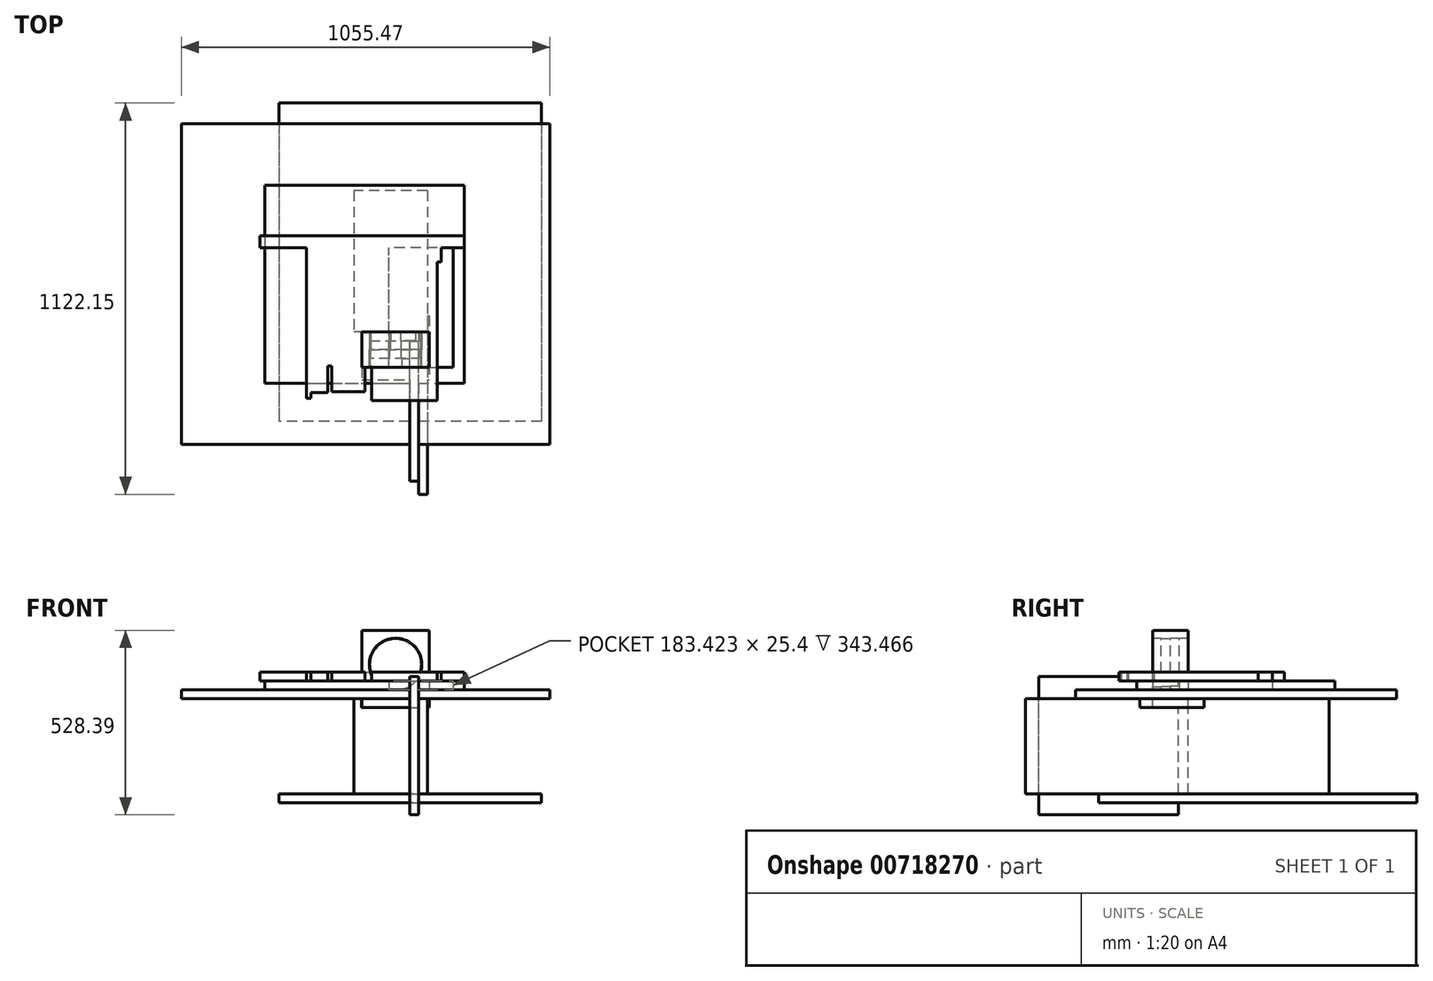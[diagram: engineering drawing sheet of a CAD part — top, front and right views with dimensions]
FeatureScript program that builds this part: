
annotation { "Feature Type Name" : "Feature", "Feature Type Description" : "" }
export const myFeature = defineFeature(function(context is Context, id is Id, definition is map)
    precondition{}
    {
        {
            var Q0;
            Q0=qCreatedBy(makeId("Front.planeOp"),FACE);
            var sketch = newSketch(context, id + "F0", { "sketchPlane" : qUnion([Q0])});
            skCircle(sketch, "E0", {"center": v(0, 0) * mm, "radius": 74.89 * mm});
            skLineSegment(sketch, "E1.bottom", {"start": v(-96.7, 97.65) * mm, "end": v(96.69, 97.65) * mm});
            skLineSegment(sketch, "E1.top", {"start": v(-96.7, -98.4) * mm, "end": v(96.69, -98.4) * mm});
            skLineSegment(sketch, "E1.left", {"start": v(-96.7, 97.65) * mm, "end": v(-96.7, -98.4) * mm});
            skLineSegment(sketch, "E1.right", {"start": v(96.69, 97.65) * mm, "end": v(96.69, -98.4) * mm});
            skSolve(sketch);
        }
        {
            var Q0;
            Q0 = qSketchRegion(id + "F0", true);
            extrude(context, id + "F1", {"entities" : qUnion([Q0]), "depth" : 25.4 * mm, "offsetDistance" : 25.4 * mm});
        }
        {
            var Q0;
            Q0=makeQuery(id+"F1.opExtrude","CAP_FACE",FACE,{"disambiguationData":[OSD([sQuery(id+"F0.wireOp",EDGE,"E0"),sQuery(id+"F0.wireOp",EDGE,"E1.bottom"),sQuery(id+"F0.wireOp",EDGE,"E1.top"),sQuery(id+"F0.wireOp",EDGE,"E1.left"),sQuery(id+"F0.wireOp",EDGE,"E1.right")])],"isStart":true});
            var sketch = newSketch(context, id + "F2", { "sketchPlane" : qUnion([Q0])});
            skLineSegment(sketch, "E2.bottom", {"start": v(96.7, 97.65) * mm, "end": v(-96.69, 97.65) * mm});
            skLineSegment(sketch, "E2.top", {"start": v(96.7, -98.4) * mm, "end": v(-96.69, -98.4) * mm});
            skLineSegment(sketch, "E2.left", {"start": v(96.7, 97.65) * mm, "end": v(96.7, -98.4) * mm});
            skLineSegment(sketch, "E2.right", {"start": v(-96.69, 97.65) * mm, "end": v(-96.69, -98.4) * mm});
            skCircle(sketch, "E3", {"center": v(0, 0) * mm, "radius": 74.66 * mm});
            skSolve(sketch);
        }
        {
            var Q0;
            Q0 = qSketchRegion(id + "F2", true);
            extrude(context, id + "F3", {"entities" : qUnion([Q0]), "operationType" : NewBodyOperationType.ADD, "depth" : 25.4 * mm, "offsetDistance" : 25.4 * mm});
        }
        {
            var Q0;
            Q0=makeQuery(id+"F3.opExtrude","CAP_FACE",FACE,{"disambiguationData":[OSD([sQuery(id+"F2.wireOp",EDGE,"E2.bottom"),sQuery(id+"F2.wireOp",EDGE,"E2.top"),sQuery(id+"F2.wireOp",EDGE,"E2.left"),sQuery(id+"F2.wireOp",EDGE,"E2.right"),sQuery(id+"F2.wireOp",EDGE,"E3")])],"isStart":false});
            var sketch = newSketch(context, id + "F4", { "sketchPlane" : qUnion([Q0])});
            skLineSegment(sketch, "E4.bottom", {"start": v(-96.69, 97.65) * mm, "end": v(96.7, 97.65) * mm});
            skLineSegment(sketch, "E4.top", {"start": v(-96.69, -98.4) * mm, "end": v(96.7, -98.4) * mm});
            skLineSegment(sketch, "E4.left", {"start": v(-96.69, 97.65) * mm, "end": v(-96.69, -98.4) * mm});
            skLineSegment(sketch, "E4.right", {"start": v(96.7, 97.65) * mm, "end": v(96.7, -98.4) * mm});
            skCircle(sketch, "E5", {"center": v(0, 0) * mm, "radius": 74.39 * mm});
            skLineSegment(sketch, "E6.bottom", {"start": v(-96.69, 97.65) * mm, "end": v(79.45, 97.65) * mm});
            skLineSegment(sketch, "E6.top", {"start": v(-96.69, -98.4) * mm, "end": v(79.45, -98.4) * mm});
            skLineSegment(sketch, "E6.right", {"start": v(79.45, 97.65) * mm, "end": v(79.45, -98.4) * mm});
            skSolve(sketch);
        }
        {
            var Q0;
            Q0 = qSketchRegion(id + "F4", true);
            extrude(context, id + "F5", {"entities" : qUnion([Q0]), "operationType" : NewBodyOperationType.ADD, "depth" : 25.4 * mm, "offsetDistance" : 25.4 * mm});
        }
        {
            var Q0;
            Q0=makeQuery(id+"F1.opExtrude","CAP_FACE",FACE,{"disambiguationData":[OSD([sQuery(id+"F0.wireOp",EDGE,"E0"),sQuery(id+"F0.wireOp",EDGE,"E1.bottom"),sQuery(id+"F0.wireOp",EDGE,"E1.top"),sQuery(id+"F0.wireOp",EDGE,"E1.left"),sQuery(id+"F0.wireOp",EDGE,"E1.right")])],"isStart":false});
            var sketch = newSketch(context, id + "F6", { "sketchPlane" : qUnion([Q0])});
            skCircle(sketch, "E7", {"center": v(0, 0) * mm, "radius": 75.35 * mm});
            skLineSegment(sketch, "E8.bottom", {"start": v(96.69, -98.4) * mm, "end": v(-96.7, -98.4) * mm});
            skLineSegment(sketch, "E8.top", {"start": v(96.69, 97.65) * mm, "end": v(-96.7, 97.65) * mm});
            skLineSegment(sketch, "E8.left", {"start": v(96.69, -98.4) * mm, "end": v(96.69, 97.65) * mm});
            skLineSegment(sketch, "E8.right", {"start": v(-96.7, -98.4) * mm, "end": v(-96.7, 97.65) * mm});
            skSolve(sketch);
        }
        {
            var Q0;
            Q0 = qSketchRegion(id + "F6", true);
            extrude(context, id + "F7", {"entities" : qUnion([Q0]), "operationType" : NewBodyOperationType.ADD, "depth" : 25.4 * mm, "offsetDistance" : 25.4 * mm});
        }
        {
            var Q0;
            Q0=makeQuery(id+"F7.boolean.opBoolean","MERGE",FACE,{"derivedFrom":[makeQuery(id+"F5.boolean.opBoolean","MERGE",FACE,{"derivedFrom":[makeQuery(id+"F3.boolean.opBoolean","MERGE",FACE,{"derivedFrom":[makeQuery(id+"F1.opExtrude","SWEPT_FACE",FACE,{"disambiguationData":[OSD([sQuery(id+"F0.wireOp",EDGE,"E1.top")])]}),makeQuery(id+"F3.opExtrude","SWEPT_FACE",FACE,{"disambiguationData":[OSD([sQuery(id+"F2.wireOp",EDGE,"E2.top")])]})]}),makeQuery(id+"F5.opExtrude","SWEPT_FACE",FACE,{"disambiguationData":[OSD([sQuery(id+"F4.wireOp",EDGE,"E4.top"),sQuery(id+"F4.wireOp",EDGE,"E6.top")])]})]}),makeQuery(id+"F7.opExtrude","SWEPT_FACE",FACE,{"disambiguationData":[OSD([sQuery(id+"F6.wireOp",EDGE,"E8.bottom")])]})]});
            var sketch = newSketch(context, id + "F8", { "sketchPlane" : qUnion([Q0])});
            skLineSegment(sketch, "E9.bottom", {"start": v(-96.7, 50.8) * mm, "end": v(96.76, 50.8) * mm});
            skLineSegment(sketch, "E9.top", {"start": v(-96.7, 86.52) * mm, "end": v(96.76, 86.52) * mm});
            skLineSegment(sketch, "E9.left", {"start": v(-96.7, 50.8) * mm, "end": v(-96.7, 86.52) * mm});
            skLineSegment(sketch, "E9.right", {"start": v(96.76, 50.8) * mm, "end": v(96.76, 86.52) * mm});
            skLineSegment(sketch, "E10.bottom", {"start": v(96.76, 50.8) * mm, "end": v(-97.9, 50.8) * mm});
            skLineSegment(sketch, "E10.top", {"start": v(96.76, -97.27) * mm, "end": v(-97.9, -97.27) * mm});
            skLineSegment(sketch, "E10.left", {"start": v(96.76, 50.8) * mm, "end": v(96.76, -97.27) * mm});
            skLineSegment(sketch, "E10.right", {"start": v(-97.9, 50.8) * mm, "end": v(-97.9, -97.27) * mm});
            skSolve(sketch);
        }
        {
            var Q0;
            Q0 = qSketchRegion(id + "F8", true);
            extrude(context, id + "F9", {"entities" : qUnion([Q0]), "operationType" : NewBodyOperationType.ADD, "depth" : 25.4 * mm, "offsetDistance" : 25.4 * mm});
        }
        {
            var Q0;
            Q0=makeQuery(id+"F5.opExtrude","CAP_FACE",FACE,{"disambiguationData":[OSD([sQuery(id+"F4.wireOp",EDGE,"E4.bottom"),sQuery(id+"F4.wireOp",EDGE,"E4.top"),sQuery(id+"F4.wireOp",EDGE,"E4.right"),sQuery(id+"F4.wireOp",EDGE,"E5"),sQuery(id+"F4.wireOp",EDGE,"E6.bottom"),sQuery(id+"F4.wireOp",EDGE,"E6.top"),sQuery(id+"F4.wireOp",EDGE,"E4.left")])],"isStart":false});
            var sketch = newSketch(context, id + "F10", { "sketchPlane" : qUnion([Q0])});
            skPoint(sketch, "E11.oppositeSnap0", {"position": v(0, -98.4) * mm});
            skLineSegment(sketch, "E11.bottom", {"start": v(-65.78, -371.3) * mm, "end": v(119.1, -371.3) * mm});
            skLineSegment(sketch, "E11.top", {"start": v(-65.78, -98.4) * mm, "end": v(119.1, -98.4) * mm});
            skLineSegment(sketch, "E11.left", {"start": v(-65.78, -371.3) * mm, "end": v(-65.78, -98.4) * mm});
            skLineSegment(sketch, "E11.right", {"start": v(119.1, -371.3) * mm, "end": v(119.1, -98.4) * mm});
            skLineSegment(sketch, "E12.bottom", {"start": v(-65.78, -98.4) * mm, "end": v(-65.78, -98.4) * mm});
            skLineSegment(sketch, "E12.top", {"start": v(-65.78, -350.33) * mm, "end": v(-65.78, -350.33) * mm});
            skLineSegment(sketch, "E12.left", {"start": v(-65.78, -98.4) * mm, "end": v(-65.78, -350.33) * mm});
            skLineSegment(sketch, "E12.right", {"start": v(-65.78, -98.4) * mm, "end": v(-65.78, -350.33) * mm});
            skSolve(sketch);
        }
        {
            var Q0;
            Q0 = qSketchRegion(id + "F10", true);
            extrude(context, id + "F11", {"entities" : qUnion([Q0]), "operationType" : NewBodyOperationType.ADD, "depth" : 404.62 * mm, "offsetDistance" : 25.4 * mm});
        }
        {
            var Q0;
            Q0=makeQuery(id+"F11.boolean.opBoolean","MERGE",FACE,{"derivedFrom":[makeQuery(id+"F9.opExtrude","CAP_FACE",FACE,{"disambiguationData":[OSD([sQuery(id+"F8.wireOp",EDGE,"E9.top"),sQuery(id+"F8.wireOp",EDGE,"E9.left"),sQuery(id+"F8.wireOp",EDGE,"E9.right"),sQuery(id+"F8.wireOp",EDGE,"E10.bottom"),sQuery(id+"F8.wireOp",EDGE,"E10.top"),sQuery(id+"F8.wireOp",EDGE,"E10.left"),sQuery(id+"F8.wireOp",EDGE,"E10.right")])],"isStart":true}),makeQuery(id+"F11.opExtrude","SWEPT_FACE",FACE,{"disambiguationData":[OSD([sQuery(id+"F10.wireOp",EDGE,"E11.top")])]})]});
            var sketch = newSketch(context, id + "F12", { "sketchPlane" : qUnion([Q0])});
            skLineSegment(sketch, "E13.bottom", {"start": v(442, 647.7) * mm, "end": v(-613.47, 647.7) * mm});
            skLineSegment(sketch, "E13.top", {"start": v(442, -271.27) * mm, "end": v(-613.47, -271.27) * mm});
            skLineSegment(sketch, "E13.left", {"start": v(442, 647.7) * mm, "end": v(442, -271.27) * mm});
            skLineSegment(sketch, "E13.right", {"start": v(-613.47, 647.7) * mm, "end": v(-613.47, -271.27) * mm});
            skSolve(sketch);
        }
        {
            var Q0;
            Q0 = qSketchRegion(id + "F12", true);
            extrude(context, id + "F13", {"entities" : qUnion([Q0]), "operationType" : NewBodyOperationType.ADD, "depth" : 25.4 * mm, "offsetDistance" : 25.4 * mm});
        }
        {
            var Q0;
            Q0=makeQuery(id+"F11.opExtrude","SWEPT_FACE",FACE,{"disambiguationData":[OSD([sQuery(id+"F10.wireOp",EDGE,"E11.bottom")])]});
            var sketch = newSketch(context, id + "F14", { "sketchPlane" : qUnion([Q0])});
            skLineSegment(sketch, "E14.bottom", {"start": v(418.46, -707.28) * mm, "end": v(-334.36, -707.28) * mm});
            skLineSegment(sketch, "E14.top", {"start": v(418.46, 205.48) * mm, "end": v(-334.36, 205.48) * mm});
            skLineSegment(sketch, "E14.left", {"start": v(418.46, -707.28) * mm, "end": v(418.46, 205.48) * mm});
            skLineSegment(sketch, "E14.right", {"start": v(-334.36, -707.28) * mm, "end": v(-334.36, 205.48) * mm});
            skSolve(sketch);
        }
        {
            var Q0;
            Q0 = qSketchRegion(id + "F14", true);
            extrude(context, id + "F15", {"entities" : qUnion([Q0]), "operationType" : NewBodyOperationType.ADD, "depth" : 25.4 * mm, "offsetDistance" : 25.4 * mm});
        }
        {
            var Q0;
            Q0=makeQuery(id+"F11.opExtrude","SWEPT_FACE",FACE,{"disambiguationData":[OSD([sQuery(id+"F10.wireOp",EDGE,"E11.left"),sQuery(id+"F10.wireOp",EDGE,"E12.right")])]});
            var sketch = newSketch(context, id + "F16", { "sketchPlane" : qUnion([Q0])});
            skLineSegment(sketch, "E15.bottom", {"start": v(455.42, -98.4) * mm, "end": v(-414.87, -98.4) * mm});
            skLineSegment(sketch, "E15.top", {"start": v(455.42, -371.3) * mm, "end": v(-414.87, -371.3) * mm});
            skLineSegment(sketch, "E15.left", {"start": v(455.42, -98.4) * mm, "end": v(455.42, -371.3) * mm});
            skLineSegment(sketch, "E15.right", {"start": v(-414.87, -98.4) * mm, "end": v(-414.87, -371.3) * mm});
            skSolve(sketch);
        }
        {
            var Q0;
            Q0 = qSketchRegion(id + "F16", true);
            extrude(context, id + "F17", {"entities" : qUnion([Q0]), "operationType" : NewBodyOperationType.ADD, "depth" : 25.4 * mm, "offsetDistance" : 25.4 * mm});
        }
        {
            var Q0;
            Q0=makeQuery(id+"F17.opExtrude","CAP_FACE",FACE,{"disambiguationData":[OSD([sQuery(id+"F16.wireOp",EDGE,"E15.bottom"),sQuery(id+"F16.wireOp",EDGE,"E15.top"),sQuery(id+"F16.wireOp",EDGE,"E15.left"),sQuery(id+"F16.wireOp",EDGE,"E15.right")])],"isStart":true});
            var sketch = newSketch(context, id + "F18", { "sketchPlane" : qUnion([Q0])});
            skLineSegment(sketch, "E16.bottom", {"start": v(377, -430.74) * mm, "end": v(-23.69, -430.74) * mm});
            skLineSegment(sketch, "E16.top", {"start": v(377, -35.11) * mm, "end": v(-23.69, -35.11) * mm});
            skLineSegment(sketch, "E16.left", {"start": v(377, -430.74) * mm, "end": v(377, -35.11) * mm});
            skLineSegment(sketch, "E16.right", {"start": v(-23.69, -430.74) * mm, "end": v(-23.69, -35.11) * mm});
            skSolve(sketch);
        }
        {
            var Q0;
            Q0 = qSketchRegion(id + "F18", true);
            extrude(context, id + "F19", {"entities" : qUnion([Q0]), "operationType" : NewBodyOperationType.ADD, "depth" : 25.4 * mm, "offsetDistance" : 25.4 * mm});
        }
        {
            var Q0;
            Q0=makeQuery(id+"F13.opExtrude","CAP_FACE",FACE,{"disambiguationData":[OSD([sQuery(id+"F12.wireOp",EDGE,"E13.bottom"),sQuery(id+"F12.wireOp",EDGE,"E13.top"),sQuery(id+"F12.wireOp",EDGE,"E13.left"),sQuery(id+"F12.wireOp",EDGE,"E13.right")])],"isStart":false});
            var sketch = newSketch(context, id + "F20", { "sketchPlane" : qUnion([Q0])});
            skLineSegment(sketch, "E17.bottom", {"start": v(-18.7, -50.8) * mm, "end": v(129.85, -50.8) * mm});
            skLineSegment(sketch, "E17.top", {"start": v(-18.7, 275.13) * mm, "end": v(129.85, 275.13) * mm});
            skLineSegment(sketch, "E17.left", {"start": v(-18.7, -50.8) * mm, "end": v(-18.7, 275.13) * mm});
            skLineSegment(sketch, "E17.right", {"start": v(129.85, -50.8) * mm, "end": v(129.85, 275.13) * mm});
            skLineSegment(sketch, "E18.bottom", {"start": v(40.38, -50.8) * mm, "end": v(164.73, -50.8) * mm});
            skLineSegment(sketch, "E18.top", {"start": v(40.38, 292.67) * mm, "end": v(164.73, 292.67) * mm});
            skLineSegment(sketch, "E18.left", {"start": v(40.38, -50.8) * mm, "end": v(40.38, 292.67) * mm});
            skLineSegment(sketch, "E18.right", {"start": v(164.73, -50.8) * mm, "end": v(164.73, 292.67) * mm});
            skLineSegment(sketch, "E19.bottom", {"start": v(40.38, 292.67) * mm, "end": v(-18.7, 292.67) * mm});
            skLineSegment(sketch, "E19.top", {"start": v(40.38, -50.8) * mm, "end": v(-18.7, -50.8) * mm});
            skLineSegment(sketch, "E19.left", {"start": v(40.38, 292.67) * mm, "end": v(40.38, -50.8) * mm});
            skLineSegment(sketch, "E19.right", {"start": v(-18.7, 292.67) * mm, "end": v(-18.7, -50.8) * mm});
            skLineSegment(sketch, "E20.bottom", {"start": v(-374.6, 471.3) * mm, "end": v(197.19, 471.3) * mm});
            skLineSegment(sketch, "E20.top", {"start": v(-374.6, -96.06) * mm, "end": v(197.19, -96.06) * mm});
            skLineSegment(sketch, "E20.left", {"start": v(-374.6, 471.3) * mm, "end": v(-374.6, -96.06) * mm});
            skLineSegment(sketch, "E20.right", {"start": v(197.19, 471.3) * mm, "end": v(197.19, -96.06) * mm});
            skSolve(sketch);
        }
        {
            var Q0;
            Q0 = qSketchRegion(id + "F20", true);
            extrude(context, id + "F21", {"entities" : qUnion([Q0]), "operationType" : NewBodyOperationType.ADD, "depth" : 25.4 * mm, "offsetDistance" : 25.4 * mm});
        }
        {
            var Q0;
            Q0=makeQuery(id+"F21.opExtrude","CAP_FACE",FACE,{"disambiguationData":[OSD([sQuery(id+"F20.wireOp",EDGE,"E18.bottom"),sQuery(id+"F20.wireOp",EDGE,"E18.top"),sQuery(id+"F20.wireOp",EDGE,"E18.right"),sQuery(id+"F20.wireOp",EDGE,"E19.bottom"),sQuery(id+"F20.wireOp",EDGE,"E19.top"),sQuery(id+"F20.wireOp",EDGE,"E19.right"),sQuery(id+"F20.wireOp",EDGE,"E20.bottom"),sQuery(id+"F20.wireOp",EDGE,"E20.top"),sQuery(id+"F20.wireOp",EDGE,"E20.left"),sQuery(id+"F20.wireOp",EDGE,"E20.right")])],"isStart":false});
            var sketch = newSketch(context, id + "F22", { "sketchPlane" : qUnion([Q0])});
            skPoint(sketch, "E21.firstSnap0", {"position": v(-76.93, 50.8) * mm});
            skLineSegment(sketch, "E21.bottom", {"start": v(-76.93, 25.4) * mm, "end": v(112.19, 25.4) * mm});
            skLineSegment(sketch, "E21.top", {"start": v(-76.93, 292.67) * mm, "end": v(112.19, 292.67) * mm});
            skLineSegment(sketch, "E21.left", {"start": v(-76.93, 25.4) * mm, "end": v(-76.93, 292.67) * mm});
            skLineSegment(sketch, "E21.right", {"start": v(112.19, 25.4) * mm, "end": v(112.19, 292.67) * mm});
            skLineSegment(sketch, "E22.bottom", {"start": v(-57.16, 313.55) * mm, "end": v(-249.49, 313.55) * mm});
            skLineSegment(sketch, "E22.top", {"start": v(-57.16, 244) * mm, "end": v(-249.49, 244) * mm});
            skLineSegment(sketch, "E22.left", {"start": v(-57.16, 313.55) * mm, "end": v(-57.16, 244) * mm});
            skLineSegment(sketch, "E22.right", {"start": v(-249.49, 313.55) * mm, "end": v(-249.49, 244) * mm});
            skSolve(sketch);
        }
        {
            var Q0;
            {var subQ73=sQuery(id+"F22.wireOp",EDGE,"E22.bottom");Q0=makeQuery(id+"F22.imprint","IMPRINT",FACE,{"disambiguationData":[TD([[makeQuery(id+"F22.imprint","IMPRINT",EDGE,{"derivedFrom":subQ73}),-1.0]])]});}
            var sketch = newSketch(context, id + "F23", { "sketchPlane" : qUnion([Q0])});
            skLineSegment(sketch, "E23.bottom", {"start": v(119.3, 292.35) * mm, "end": v(-255.69, 292.35) * mm});
            skLineSegment(sketch, "E23.top", {"start": v(119.3, -40.38) * mm, "end": v(-255.69, -40.38) * mm});
            skLineSegment(sketch, "E23.left", {"start": v(119.3, 292.35) * mm, "end": v(119.3, -40.38) * mm});
            skLineSegment(sketch, "E23.right", {"start": v(-255.69, 292.35) * mm, "end": v(-255.69, -40.38) * mm});
            skPoint(sketch, "E24.oppositeSnap0", {"position": v(-68.2, 292.35) * mm});
            skLineSegment(sketch, "E24.bottom", {"start": v(119.3, -40.38) * mm, "end": v(-68.2, -40.38) * mm});
            skLineSegment(sketch, "E24.top", {"start": v(119.3, -146.15) * mm, "end": v(-68.2, -146.15) * mm});
            skLineSegment(sketch, "E24.left", {"start": v(119.3, -40.38) * mm, "end": v(119.3, -146.15) * mm});
            skLineSegment(sketch, "E24.right", {"start": v(-68.2, -40.38) * mm, "end": v(-68.2, -146.15) * mm});
            skLineSegment(sketch, "E25.bottom", {"start": v(-242.38, -140.03) * mm, "end": v(-255.69, -140.03) * mm});
            skLineSegment(sketch, "E25.top", {"start": v(-242.38, 292.35) * mm, "end": v(-255.69, 292.35) * mm});
            skLineSegment(sketch, "E25.left", {"start": v(-242.38, -140.03) * mm, "end": v(-242.38, 292.35) * mm});
            skLineSegment(sketch, "E25.right", {"start": v(-255.69, -140.03) * mm, "end": v(-255.69, 292.35) * mm});
            skLineSegment(sketch, "E26.bottom", {"start": v(119.3, 292.35) * mm, "end": v(197.3, 292.35) * mm});
            skLineSegment(sketch, "E26.top", {"start": v(119.3, 326.83) * mm, "end": v(197.3, 326.83) * mm});
            skLineSegment(sketch, "E26.left", {"start": v(119.3, 292.35) * mm, "end": v(119.3, 326.83) * mm});
            skLineSegment(sketch, "E26.right", {"start": v(197.3, 292.35) * mm, "end": v(197.3, 326.83) * mm});
            skLineSegment(sketch, "E27.bottom", {"start": v(119.3, 326.83) * mm, "end": v(-389.01, 326.83) * mm});
            skLineSegment(sketch, "E27.top", {"start": v(119.3, 292.35) * mm, "end": v(-389.01, 292.35) * mm});
            skLineSegment(sketch, "E27.left", {"start": v(119.3, 326.83) * mm, "end": v(119.3, 292.35) * mm});
            skLineSegment(sketch, "E27.right", {"start": v(-389.01, 326.83) * mm, "end": v(-389.01, 292.35) * mm});
            skSolve(sketch);
        }
        {
            var Q0;
            Q0 = qSketchRegion(id + "F23", true);
            extrude(context, id + "F24", {"entities" : qUnion([Q0]), "operationType" : NewBodyOperationType.ADD, "depth" : 25.4 * mm, "offsetDistance" : 25.4 * mm});
        }
        {
            var Q0;
            {var subQ73=sQuery(id+"F22.wireOp",EDGE,"E22.bottom");Q0=makeQuery(id+"F22.imprint","IMPRINT",FACE,{"disambiguationData":[TD([[makeQuery(id+"F22.imprint","IMPRINT",EDGE,{"derivedFrom":subQ73}),-1.0]])]});}
            var sketch = newSketch(context, id + "F25", { "sketchPlane" : qUnion([Q0])});
            skLineSegment(sketch, "E28.bottom", {"start": v(0, 0) * mm, "end": v(-69.9, 0) * mm});
            skLineSegment(sketch, "E28.top", {"start": v(0, 301.84) * mm, "end": v(-69.9, 301.84) * mm});
            skLineSegment(sketch, "E28.left", {"start": v(0, 0) * mm, "end": v(0, 301.84) * mm});
            skLineSegment(sketch, "E28.right", {"start": v(-69.9, 0) * mm, "end": v(-69.9, 301.84) * mm});
            skLineSegment(sketch, "E29.bottom", {"start": v(0, 301.84) * mm, "end": v(131.1, 301.84) * mm});
            skLineSegment(sketch, "E29.top", {"start": v(0, 251.58) * mm, "end": v(131.1, 251.58) * mm});
            skLineSegment(sketch, "E29.left", {"start": v(0, 301.84) * mm, "end": v(0, 251.58) * mm});
            skLineSegment(sketch, "E29.right", {"start": v(131.1, 301.84) * mm, "end": v(131.1, 251.58) * mm});
            skLineSegment(sketch, "E30.bottom", {"start": v(-69.9, 301.84) * mm, "end": v(-248.72, 301.84) * mm});
            skLineSegment(sketch, "E30.top", {"start": v(-69.9, 239.47) * mm, "end": v(-248.72, 239.47) * mm});
            skLineSegment(sketch, "E30.left", {"start": v(-69.9, 301.84) * mm, "end": v(-69.9, 239.47) * mm});
            skLineSegment(sketch, "E30.right", {"start": v(-248.72, 301.84) * mm, "end": v(-248.72, 239.47) * mm});
            skLineSegment(sketch, "E31.bottom", {"start": v(101.54, 0) * mm, "end": v(0, 0) * mm});
            skLineSegment(sketch, "E31.top", {"start": v(101.54, 301.84) * mm, "end": v(0, 301.84) * mm});
            skLineSegment(sketch, "E31.left", {"start": v(101.54, 0) * mm, "end": v(101.54, 301.84) * mm});
            skLineSegment(sketch, "E32.bottom", {"start": v(-69.9, 0) * mm, "end": v(101.54, 0) * mm});
            skLineSegment(sketch, "E32.top", {"start": v(-69.9, -46.32) * mm, "end": v(101.54, -46.32) * mm});
            skLineSegment(sketch, "E32.left", {"start": v(-69.9, 0) * mm, "end": v(-69.9, -46.32) * mm});
            skLineSegment(sketch, "E32.right", {"start": v(101.54, 0) * mm, "end": v(101.54, -46.32) * mm});
            skLineSegment(sketch, "E33.bottom", {"start": v(-69.9, -46.32) * mm, "end": v(-69.9, -46.32) * mm});
            skLineSegment(sketch, "E33.top", {"start": v(-69.9, 239.47) * mm, "end": v(-69.9, 239.47) * mm});
            skLineSegment(sketch, "E33.left", {"start": v(-69.9, -46.32) * mm, "end": v(-69.9, 239.47) * mm});
            skLineSegment(sketch, "E33.right", {"start": v(-69.9, -46.32) * mm, "end": v(-69.9, 239.47) * mm});
            skLineSegment(sketch, "E34.bottom", {"start": v(-69.9, -46.32) * mm, "end": v(-116.6, -46.32) * mm});
            skLineSegment(sketch, "E34.top", {"start": v(-69.9, 239.47) * mm, "end": v(-116.6, 239.47) * mm});
            skLineSegment(sketch, "E34.right", {"start": v(-116.6, -46.32) * mm, "end": v(-116.6, 239.47) * mm});
            skLineSegment(sketch, "E35.bottom", {"start": v(-116.6, -46.32) * mm, "end": v(-248.72, -46.32) * mm});
            skLineSegment(sketch, "E35.top", {"start": v(-116.6, 239.47) * mm, "end": v(-248.72, 239.47) * mm});
            skLineSegment(sketch, "E35.right", {"start": v(-248.72, -46.32) * mm, "end": v(-248.72, 239.47) * mm});
            skLineSegment(sketch, "E36.bottom", {"start": v(-182.65, -46.32) * mm, "end": v(-88.03, -46.32) * mm});
            skLineSegment(sketch, "E36.top", {"start": v(-182.65, -120.33) * mm, "end": v(-88.03, -120.33) * mm});
            skLineSegment(sketch, "E36.left", {"start": v(-182.65, -46.32) * mm, "end": v(-182.65, -120.33) * mm});
            skLineSegment(sketch, "E36.right", {"start": v(-88.03, -46.32) * mm, "end": v(-88.03, -120.33) * mm});
            skLineSegment(sketch, "E37.bottom", {"start": v(-194.12, -123.05) * mm, "end": v(-248.72, -123.05) * mm});
            skLineSegment(sketch, "E37.top", {"start": v(-194.12, -46.32) * mm, "end": v(-248.72, -46.32) * mm});
            skLineSegment(sketch, "E37.left", {"start": v(-194.12, -123.05) * mm, "end": v(-194.12, -46.32) * mm});
            skLineSegment(sketch, "E37.right", {"start": v(-248.72, -123.05) * mm, "end": v(-248.72, -46.32) * mm});
            skSolve(sketch);
        }
        {
            var Q0;
            Q0 = qSketchRegion(id + "F25", true);
            extrude(context, id + "F26", {"entities" : qUnion([Q0]), "operationType" : NewBodyOperationType.ADD, "depth" : 25.4 * mm, "offsetDistance" : 25.4 * mm});
        }
    });
